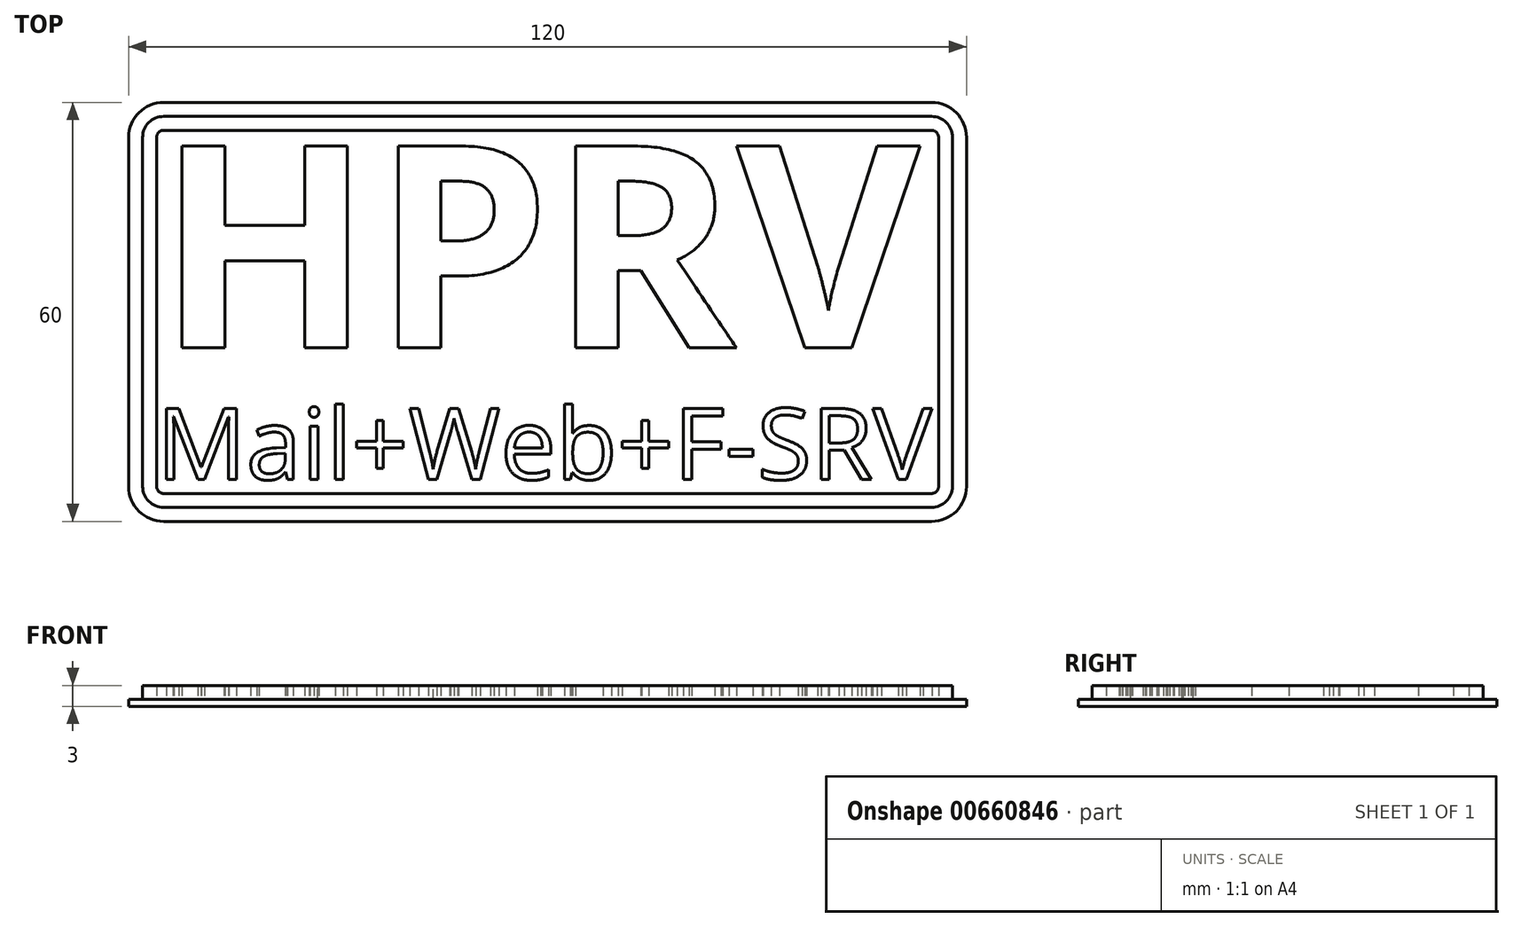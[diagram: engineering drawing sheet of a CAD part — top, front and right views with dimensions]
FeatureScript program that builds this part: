
annotation { "Feature Type Name" : "Feature", "Feature Type Description" : "" }
export const myFeature = defineFeature(function(context is Context, id is Id, definition is map)
    precondition{}
    {
        {
            assignVariable(context, id + "F0", {"variableType" : VariableType.LENGTH, "name" : "st", "lengthValue" : 1 * mm});
        }
        {
            assignVariable(context, id + "F1", {"variableType" : VariableType.LENGTH, "name" : "ft", "lengthValue" : 2 * mm});
        }
        {
            var Q0;
            Q0=qCreatedBy(makeId("Top.planeOp"),FACE);
            var sketch = newSketch(context, id + "F2", { "sketchPlane" : qUnion([Q0])});
            skLineSegment(sketch, "E0.bottom", {"start": v(-55, 30) * mm, "end": v(55, 30) * mm});
            skLineSegment(sketch, "E0.top", {"start": v(-55, -30) * mm, "end": v(55, -30) * mm});
            skLineSegment(sketch, "E0.left", {"start": v(-60, 25) * mm, "end": v(-60, -25) * mm});
            skLineSegment(sketch, "E0.right", {"start": v(60, 25) * mm, "end": v(60, -25) * mm});
            skPoint(sketch, "E1", {"position": v(0, 30) * mm});
            skPoint(sketch, "E2", {"position": v(-60, 0) * mm});
            skPoint(sketch, "E3.visualSharp", {"position": v(-60, 30) * mm});
            skArc(sketch, "E3.filletArc", {"start": v(-55, 30) * mm, "mid": v(-58.54, 28.54) * mm, "end": v(-60, 25) * mm});
            skPoint(sketch, "E4.visualSharp", {"position": v(60, 30) * mm});
            skArc(sketch, "E4.filletArc", {"start": v(60, 25) * mm, "mid": v(58.54, 28.54) * mm, "end": v(55, 30) * mm});
            skPoint(sketch, "E5.visualSharp", {"position": v(60, -30) * mm});
            skArc(sketch, "E5.filletArc", {"start": v(55, -30) * mm, "mid": v(58.54, -28.54) * mm, "end": v(60, -25) * mm});
            skPoint(sketch, "E6.visualSharp", {"position": v(-60, -30) * mm});
            skArc(sketch, "E6.filletArc", {"start": v(-60, -25) * mm, "mid": v(-58.54, -28.54) * mm, "end": v(-55, -30) * mm});
            skSolve(sketch);
        }
        {
            var Q0;
            Q0=qSketchRegion(id+"F2",true);
            extrude(context, id + "F3", {"entities" : qUnion([Q0]), "depth" : getVariable(context, 'st'), "offsetDistance" : 25 * mm});
        }
        {
            var Q0;
            Q0=makeQuery(id+"F3.opExtrude","CAP_FACE",FACE,{"disambiguationData":[OSD([sQuery(id+"F2.wireOp",EDGE,"E0.bottom"),sQuery(id+"F2.wireOp",EDGE,"E0.top"),sQuery(id+"F2.wireOp",EDGE,"E0.left"),sQuery(id+"F2.wireOp",EDGE,"E0.right"),sQuery(id+"F2.wireOp",EDGE,"E3.filletArc"),sQuery(id+"F2.wireOp",EDGE,"E4.filletArc"),sQuery(id+"F2.wireOp",EDGE,"E5.filletArc"),sQuery(id+"F2.wireOp",EDGE,"E6.filletArc")])],"isStart":false});
            var sketch = newSketch(context, id + "F4", { "sketchPlane" : qUnion([Q0])});
            skArc(sketch, "E7.0", {"start": v(-55, 28) * mm, "mid": v(-57.12, 27.12) * mm, "end": v(-58, 25) * mm});
            skLineSegment(sketch, "E7.1", {"start": v(-55, 28) * mm, "end": v(55, 28) * mm});
            skLineSegment(sketch, "E7.2", {"start": v(-58, 25) * mm, "end": v(-58, -25) * mm});
            skArc(sketch, "E7.3", {"start": v(58, 25) * mm, "mid": v(57.12, 27.12) * mm, "end": v(55, 28) * mm});
            skArc(sketch, "E7.4", {"start": v(-58, -25) * mm, "mid": v(-57.12, -27.12) * mm, "end": v(-55, -28) * mm});
            skLineSegment(sketch, "E7.5", {"start": v(-55, -28) * mm, "end": v(55, -28) * mm});
            skArc(sketch, "E7.6", {"start": v(55, -28) * mm, "mid": v(57.12, -27.12) * mm, "end": v(58, -25) * mm});
            skLineSegment(sketch, "E7.7", {"start": v(58, 25) * mm, "end": v(58, -25) * mm});
            skArc(sketch, "E8.0", {"start": v(-55, 26) * mm, "mid": v(-55.7, 25.7) * mm, "end": v(-56, 25) * mm});
            skLineSegment(sketch, "E8.1", {"start": v(-55, 26) * mm, "end": v(55, 26) * mm});
            skLineSegment(sketch, "E8.2", {"start": v(-56, 25) * mm, "end": v(-56, -25) * mm});
            skArc(sketch, "E8.3", {"start": v(56, 25) * mm, "mid": v(55.7, 25.7) * mm, "end": v(55, 26) * mm});
            skArc(sketch, "E8.4", {"start": v(-56, -25) * mm, "mid": v(-55.7, -25.7) * mm, "end": v(-55, -26) * mm});
            skLineSegment(sketch, "E8.5", {"start": v(-55, -26) * mm, "end": v(55, -26) * mm});
            skArc(sketch, "E8.6", {"start": v(55, -26) * mm, "mid": v(55.7, -25.7) * mm, "end": v(56, -25) * mm});
            skLineSegment(sketch, "E8.7", {"start": v(56, 25) * mm, "end": v(56, -25) * mm});
            skText(sketch, "E9", { "text": "HPRV", "fontName": "OpenSans-Bold.ttf"});
            skText(sketch, "E10", { "text": "Mail+Web+F-SRV", "fontName": "OpenSans-Regular.ttf"});
            skLineSegment(sketch, "E11", {"start": v(0, -23.99) * mm, "end": v(0, 23.99) * mm, "construction": true});
            const initialGuessF4  = {"E9": [-0.056, -0.00514, 1, 0, 0.02913], "E10": [-0.056, -0.02399, 1, 0, 0.01024]};
            skSetInitialGuess(sketch, initialGuessF4);
            skSolve(sketch);
        }
        {
            var Q0;
            Q0=makeQuery(id+"F4.imprint","IMPRINT",FACE,{"disambiguationData":[TD([[makeQuery(id+"F4.imprint","IMPRINT",EDGE,{"derivedFrom":sQuery(id+"F4.wireOp",EDGE,"E10.sketch_text.stroke-215")}),-1.0]])]});
            var Q1;
            Q1=makeQuery(id+"F4.imprint","IMPRINT",FACE,{"disambiguationData":[TD([[makeQuery(id+"F4.imprint","IMPRINT",EDGE,{"derivedFrom":sQuery(id+"F4.wireOp",EDGE,"E10.sketch_text.stroke-198")}),-1.0]])]});
            var Q2;
            Q2=makeQuery(id+"F4.imprint","IMPRINT",FACE,{"disambiguationData":[TD([[makeQuery(id+"F4.imprint","IMPRINT",EDGE,{"derivedFrom":sQuery(id+"F4.wireOp",EDGE,"E10.sketch_text.stroke-178")}),-1.0]])]});
            var Q3;
            Q3=makeQuery(id+"F4.imprint","IMPRINT",FACE,{"disambiguationData":[TD([[makeQuery(id+"F4.imprint","IMPRINT",EDGE,{"derivedFrom":sQuery(id+"F4.wireOp",EDGE,"E10.sketch_text.stroke-170")}),-1.0]])]});
            var Q4;
            Q4=makeQuery(id+"F4.imprint","IMPRINT",FACE,{"disambiguationData":[TD([[makeQuery(id+"F4.imprint","IMPRINT",EDGE,{"derivedFrom":sQuery(id+"F4.wireOp",EDGE,"E10.sketch_text.stroke-145")}),-1.0]])]});
            var Q5;
            Q5=makeQuery(id+"F4.imprint","IMPRINT",FACE,{"disambiguationData":[TD([[makeQuery(id+"F4.imprint","IMPRINT",EDGE,{"derivedFrom":sQuery(id+"F4.wireOp",EDGE,"E10.sketch_text.stroke-136")}),-1.0]])]});
            var Q6;
            Q6=makeQuery(id+"F4.imprint","IMPRINT",FACE,{"disambiguationData":[TD([[makeQuery(id+"F4.imprint","IMPRINT",EDGE,{"derivedFrom":sQuery(id+"F4.wireOp",EDGE,"E10.sketch_text.stroke-128")}),-1.0]])]});
            var Q7;
            Q7=makeQuery(id+"F4.imprint","IMPRINT",FACE,{"disambiguationData":[TD([[makeQuery(id+"F4.imprint","IMPRINT",EDGE,{"derivedFrom":sQuery(id+"F4.wireOp",EDGE,"E10.sketch_text.stroke-97")}),-1.0]])]});
            var Q8;
            Q8=makeQuery(id+"F4.imprint","IMPRINT",FACE,{"disambiguationData":[TD([[makeQuery(id+"F4.imprint","IMPRINT",EDGE,{"derivedFrom":sQuery(id+"F4.wireOp",EDGE,"E10.sketch_text.stroke-72")}),-1.0]])]});
            var Q9;
            Q9=makeQuery(id+"F4.imprint","IMPRINT",FACE,{"disambiguationData":[TD([[makeQuery(id+"F4.imprint","IMPRINT",EDGE,{"derivedFrom":sQuery(id+"F4.wireOp",EDGE,"E10.sketch_text.stroke-0")}),-1.0]])]});
            var Q10;
            Q10=makeQuery(id+"F4.imprint","IMPRINT",FACE,{"disambiguationData":[TD([[makeQuery(id+"F4.imprint","IMPRINT",EDGE,{"derivedFrom":sQuery(id+"F4.wireOp",EDGE,"E10.sketch_text.stroke-9")}),-1.0]])]});
            var Q11;
            Q11=makeQuery(id+"F4.imprint","IMPRINT",FACE,{"disambiguationData":[TD([[makeQuery(id+"F4.imprint","IMPRINT",EDGE,{"derivedFrom":sQuery(id+"F4.wireOp",EDGE,"E10.sketch_text.stroke-35")}),-1.0]])]});
            var Q12;
            Q12=makeQuery(id+"F4.imprint","IMPRINT",FACE,{"disambiguationData":[TD([[makeQuery(id+"F4.imprint","IMPRINT",EDGE,{"derivedFrom":sQuery(id+"F4.wireOp",EDGE,"E10.sketch_text.stroke-55")}),-1.0]])]});
            var Q13;
            Q13=makeQuery(id+"F4.imprint","IMPRINT",FACE,{"disambiguationData":[TD([[makeQuery(id+"F4.imprint","IMPRINT",EDGE,{"derivedFrom":sQuery(id+"F4.wireOp",EDGE,"E10.sketch_text.stroke-63")}),-1.0]])]});
            var Q14;
            Q14=makeQuery(id+"F4.imprint","IMPRINT",FACE,{"disambiguationData":[TD([[makeQuery(id+"F4.imprint","IMPRINT",EDGE,{"derivedFrom":sQuery(id+"F4.wireOp",EDGE,"E9.sketch_text.stroke-0")}),-1.0]])]});
            var Q15;
            Q15=makeQuery(id+"F4.imprint","IMPRINT",FACE,{"disambiguationData":[TD([[makeQuery(id+"F4.imprint","IMPRINT",EDGE,{"derivedFrom":sQuery(id+"F4.wireOp",EDGE,"E7.0")}),1.0]])]});
            var Q16;
            Q16=makeQuery(id+"F4.imprint","IMPRINT",FACE,{"disambiguationData":[TD([[makeQuery(id+"F4.imprint","IMPRINT",EDGE,{"derivedFrom":sQuery(id+"F4.wireOp",EDGE,"E9.sketch_text.stroke-13")}),-1.0]])]});
            var Q17;
            Q17=makeQuery(id+"F4.imprint","IMPRINT",FACE,{"disambiguationData":[TD([[makeQuery(id+"F4.imprint","IMPRINT",EDGE,{"derivedFrom":sQuery(id+"F4.wireOp",EDGE,"E9.sketch_text.stroke-41")}),-1.0]])]});
            var Q18;
            Q18=makeQuery(id+"F4.imprint","IMPRINT",FACE,{"disambiguationData":[TD([[makeQuery(id+"F4.imprint","IMPRINT",EDGE,{"derivedFrom":sQuery(id+"F4.wireOp",EDGE,"E9.sketch_text.stroke-45")}),-1.0]])]});
            var Q19;
            Q19=makeQuery(id+"F4.imprint","IMPRINT",FACE,{"disambiguationData":[TD([[makeQuery(id+"F4.imprint","IMPRINT",EDGE,{"derivedFrom":sQuery(id+"F4.wireOp",EDGE,"E9.sketch_text.stroke-57")}),-1.0]])]});
            var Q20;
            Q20=makeQuery(id+"F4.imprint","IMPRINT",FACE,{"disambiguationData":[TD([[makeQuery(id+"F4.imprint","IMPRINT",EDGE,{"derivedFrom":sQuery(id+"F4.wireOp",EDGE,"E9.sketch_text.stroke-76")}),-1.0]])]});
            var Q21;
            Q21=makeQuery(id+"F4.imprint","IMPRINT",FACE,{"disambiguationData":[TD([[makeQuery(id+"F4.imprint","IMPRINT",EDGE,{"derivedFrom":sQuery(id+"F4.wireOp",EDGE,"E9.sketch_text.stroke-47")}),-1.0]])]});
            var Q22;
            Q22=makeQuery(id+"F4.imprint","IMPRINT",FACE,{"disambiguationData":[TD([[makeQuery(id+"F4.imprint","IMPRINT",EDGE,{"derivedFrom":sQuery(id+"F4.wireOp",EDGE,"E10.sketch_text.stroke-45")}),-1.0]])]});
            var Q23;
            Q23=makeQuery(id+"F4.imprint","IMPRINT",FACE,{"disambiguationData":[TD([[makeQuery(id+"F4.imprint","IMPRINT",EDGE,{"derivedFrom":sQuery(id+"F4.wireOp",EDGE,"E10.sketch_text.stroke-57")}),-1.0]])]});
            var Q24;
            Q24=makeQuery(id+"F4.imprint","IMPRINT",FACE,{"disambiguationData":[TD([[makeQuery(id+"F4.imprint","IMPRINT",EDGE,{"derivedFrom":sQuery(id+"F4.wireOp",EDGE,"E10.sketch_text.stroke-73")}),-1.0]])]});
            var Q25;
            Q25=makeQuery(id+"F4.imprint","IMPRINT",FACE,{"disambiguationData":[TD([[makeQuery(id+"F4.imprint","IMPRINT",EDGE,{"derivedFrom":sQuery(id+"F4.wireOp",EDGE,"E10.sketch_text.stroke-147")}),-1.0]])]});
            var Q26;
            Q26=makeQuery(id+"F4.imprint","IMPRINT",FACE,{"disambiguationData":[TD([[makeQuery(id+"F4.imprint","IMPRINT",EDGE,{"derivedFrom":sQuery(id+"F4.wireOp",EDGE,"E10.sketch_text.stroke-157")}),-1.0]])]});
            var Q27;
            Q27=makeQuery(id+"F4.imprint","IMPRINT",FACE,{"disambiguationData":[TD([[makeQuery(id+"F4.imprint","IMPRINT",EDGE,{"derivedFrom":sQuery(id+"F4.wireOp",EDGE,"E10.sketch_text.stroke-204")}),-1.0]])]});
            extrude(context, id + "F5", {"entities" : qUnion([Q0, Q1, Q2, Q3, Q4, Q5, Q6, Q7, Q8, Q9, Q10, Q11, Q12, Q13, Q14, Q15, Q16, Q17, Q18, Q19, Q20, Q21, Q22, Q23, Q24, Q25, Q26, Q27]), "operationType" : NewBodyOperationType.ADD, "depth" : getVariable(context, 'ft'), "offsetDistance" : 25 * mm});
        }
    });
